# Revit family: 2CKA006800A2717
name_source: partatom
category: Elektroinstallationen
revit_build: Autodesk Revit 2017 (Build: 20160225_1515(x64)
units: mm (PartAtom-declared; Revit-internal decimal feet)

## family parameters
Basisbauteil = Fläche
Beim Laden mit Abzugskörper schneiden = Nein
Bemaßung runder Anschluss = Durchmesser verwenden
Beschriftungsausrichtung beibehalten = Nein
Gemeinsam genutzt = Nein
Raumberechnungspunkt = Nein
Teiletyp = Normal

## types (1)
- 2CKA006800A2717
    Art des Test-/Pauseknopfes = Kombination
    BIM = https://media.live.bim.site
    BIMSITE_PRODUCT_ID = a27fedab923d12db55102235fc91873ee43077d5
    Beschreibung = Busch-Rauchalarm ProfessionalLINE, studioweiß, Sicherheitstechnik, Busch-Rauchalarm ProfessionalLINE, Busch-Rauchalarm ProfessionalLINE Zur Früherkennung von Schwelbränden und offenen Bränden mit Rauchentwicklung im Innenbereich nach foto-optischem Messprinzip (Tyndall). Fest eingebaute Lithiumbatterie mit einer Lebensdauer von min. 10 Jahren. Mit Testknopf und Stummschaltung. Geprüft nach DIN EN 14604. Akustischer Alarm mit 85 dBA auf 3 m. Demontagesicherung. Nicht vernetzbar. Durchmesser: 120 mm. Höhe: 47,50 mm.
    Durchmesser [m] = 0.12
    Farbe = weiß
    GTIN = 4011395186930
    Gerätebreite [mm] = 120.5
    Gerätehöhe [mm] = 47.5
    Gerätetiefe [mm] = 120.5
    Gewicht [kg/m] = 0.26
    HAN = 2CKA006800A2717
    HeinzeBIM = https://www.heinze.de
    Hersteller = Busch-Jaeger
    Höhe [mm] = 47.5
    Ist System = Nein
    Ist Zubehör = Nein
    Lautstärke [dB(A)] = 85
    Mit Sockel = Ja
    Primärstromversorgung = Batterie/Akku
    Produktseite = https://media.live.bim.site
    RAL-Nummer (ähnlich) = 9016
    Spannungsart der Versorgungsspannung = DC
    Standalone = Ja
    TYPE = 6833-84
    Typname = Busch-Rauchalarm ProfessionalLINE, studioweiß, Sicherheitstechnik, Busch-Rauchalarm ProfessionalLINE
    URL = https://www.busch-jaeger.de
    VdS anerkannt = Ja
    Vorgabe-Ansicht = 1219 mm

## geometry (parser evidence)
native form markers: Sweep x3
no freeform markers — native parametric forms only
